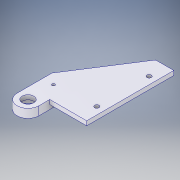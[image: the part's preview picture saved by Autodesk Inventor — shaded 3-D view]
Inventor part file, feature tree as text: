
AUTODESK INVENTOR PART (.ipt)
format: ipt  version: 2017 (Build 210142000, 142)  size: 160,768 bytes
history: native  units: in
note: dims shown in document units (in); Inventor stores cm internally (conversion verified against a paired STEP export)
features: extrude x2, sketch x2, projected_geometry x1
ambient origin geometry x8: Origin, YZ Plane, XZ Plane, XY Plane, X Axis, Y Axis, Z Axis, Center Point
bodies: Solid1 (feature_tree)
feature tree (5):
  extrude  "Extrusion1"  TaperAngle=90.0deg  [1 undecoded]
  extrude  "Extrusion3"  Depth=1.0in
  sketch  "Sketch3"  dims[d6=2.3622in d7=90.0deg]
  sketch  "Sketch6"  dims[d8=0.4929in d9=1.0in d10=0.2953in d11=0.5906in d13=0.9456in d14=0.1181in d15=0.0in d18=0.1969in d19=0.4724in d20=0.4724in d21=0.1181in d22=0.1181in d25=0.315in d26=0.4335in d27=0.2562in d28=0.0787in d29=0.0787in d31=0.4331in d32=0.0591in d33=0.2362in d34=0.1181in d35=0.2362in d36=0.0in]
  projected_geometry  "Projected Loop3"
note: 1 required parameter value undecoded (feature->parameter linkage not recoverable at this tier; creation-order binding heuristic only, values carry confidence <= 0.55)
